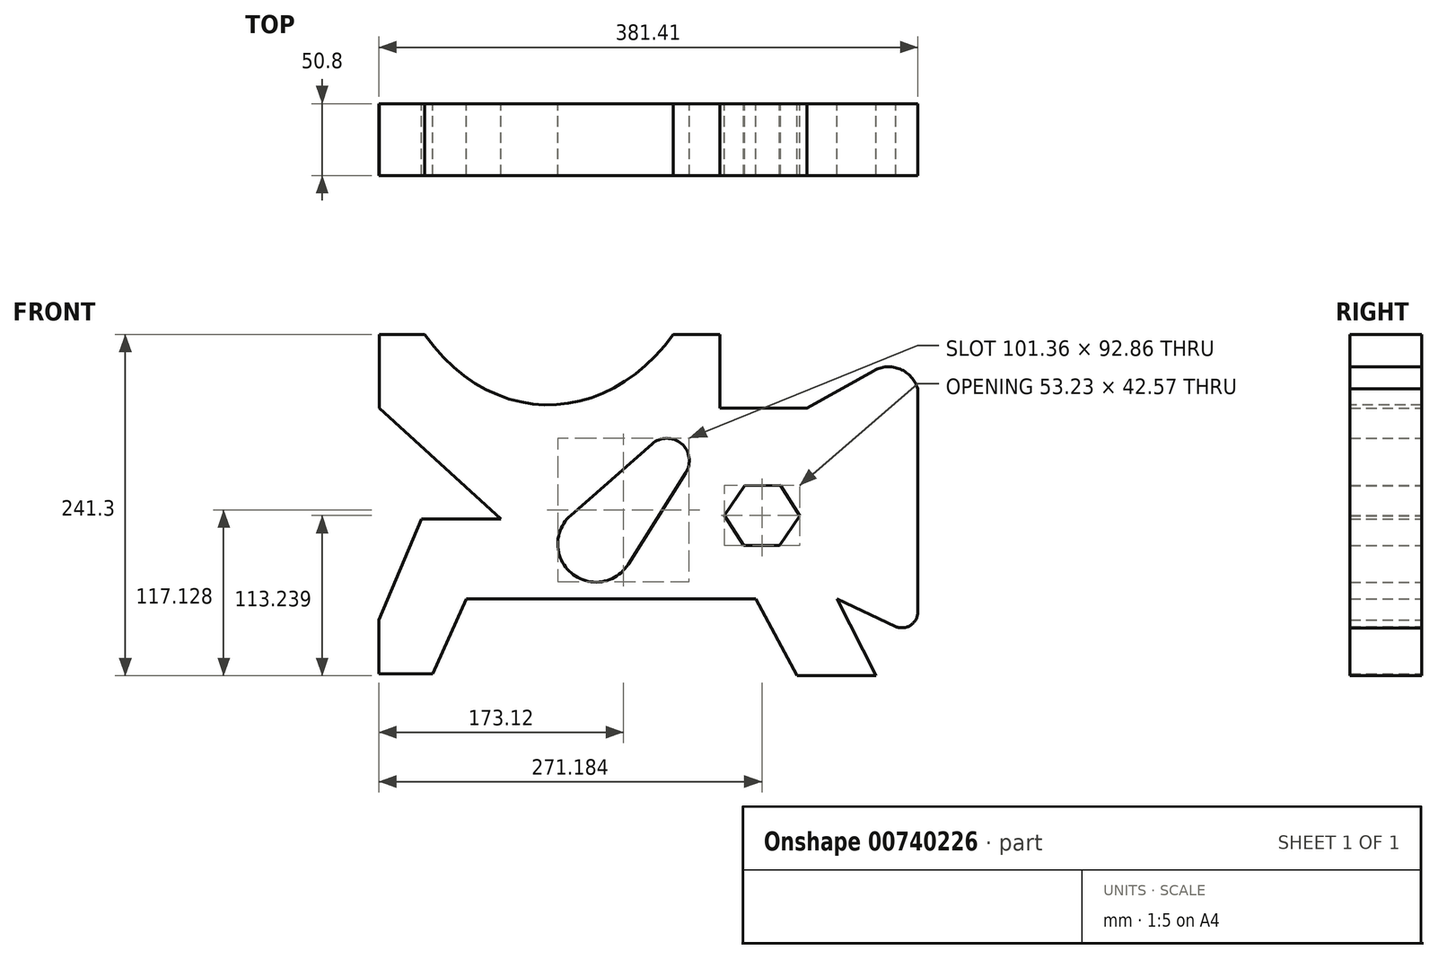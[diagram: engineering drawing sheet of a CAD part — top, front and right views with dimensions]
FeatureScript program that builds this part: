
annotation { "Feature Type Name" : "Feature", "Feature Type Description" : "" }
export const myFeature = defineFeature(function(context is Context, id is Id, definition is map)
    precondition{}
    {
        {
            var Q0;
            Q0=qCreatedBy(makeId("Front.planeOp"),FACE);
            var sketch = newSketch(context, id + "F0", { "sketchPlane" : qUnion([Q0])});
            skPoint(sketch, "E0.middle", {"position": v(-76.03, 243.1) * mm});
            skLineSegment(sketch, "E1", {"start": v(-266.94, 123.7) * mm, "end": v(-266.94, 161.8) * mm});
            skLineSegment(sketch, "E2", {"start": v(-266.94, 123.7) * mm, "end": v(-228.84, 123.7) * mm});
            skLineSegment(sketch, "E3", {"start": v(-228.84, 123.7) * mm, "end": v(-205, 176.8) * mm});
            skLineSegment(sketch, "E4", {"start": v(-266.94, 161.8) * mm, "end": v(-236.71, 233.26) * mm});
            skLineSegment(sketch, "E5", {"start": v(-236.71, 233.26) * mm, "end": v(-180.58, 233.26) * mm});
            skLineSegment(sketch, "E6", {"start": v(-180.58, 233.26) * mm, "end": v(-266.53, 311.7) * mm});
            skLineSegment(sketch, "E7", {"start": v(-266.53, 311.7) * mm, "end": v(-266.53, 363.76) * mm});
            skLineSegment(sketch, "E8", {"start": v(-266.53, 363.76) * mm, "end": v(-234.48, 363.76) * mm});
            skFitSpline(sketch, "E9", {"points": [v(-234.48, 363.76) * mm, v(-58.6, 363.76) * mm], "startDerivative": vector(146.16, -206.02) * mm, "endDerivative": vector(136.89, 191.75) * mm});
            skLineSegment(sketch, "E10", {"start": v(-58.6, 363.76) * mm, "end": v(-25.53, 363.76) * mm});
            skLineSegment(sketch, "E11", {"start": v(-25.53, 363.76) * mm, "end": v(-25.53, 311.7) * mm});
            skLineSegment(sketch, "E12", {"start": v(-25.53, 311.7) * mm, "end": v(36.19, 311.7) * mm});
            skLineSegment(sketch, "E13", {"start": v(83.32, 338.14) * mm, "end": v(36.19, 311.7) * mm});
            skArc(sketch, "E14", {"start": v(83.32, 338.14) * mm, "mid": v(102.02, 339.25) * mm, "end": v(114.47, 325.25) * mm});
            skLineSegment(sketch, "E15", {"start": v(114.47, 325.25) * mm, "end": v(114.47, 167.48) * mm});
            skArc(sketch, "E16", {"start": v(114.47, 167.48) * mm, "mid": v(109.5, 158.16) * mm, "end": v(99, 157.1) * mm});
            skLineSegment(sketch, "E17", {"start": v(99, 157.1) * mm, "end": v(57.48, 176.8) * mm});
            skLineSegment(sketch, "E18", {"start": v(57.48, 176.8) * mm, "end": v(84.93, 122.46) * mm});
            skLineSegment(sketch, "E19", {"start": v(84.93, 122.46) * mm, "end": v(28.95, 122.46) * mm});
            skLineSegment(sketch, "E20", {"start": v(28.95, 122.46) * mm, "end": v(0, 176.8) * mm});
            skLineSegment(sketch, "E21", {"start": v(-205, 176.8) * mm, "end": v(0, 176.8) * mm});
            skLineSegment(sketch, "E22", {"start": v(-73.5, 286.34) * mm, "end": v(-131.05, 235.9) * mm});
            skLineSegment(sketch, "E23", {"start": v(-90.41, 201.21) * mm, "end": v(-49.64, 265.97) * mm});
            skArc(sketch, "E24", {"start": v(-73.5, 286.34) * mm, "mid": v(-52.77, 286.48) * mm, "end": v(-49.64, 265.97) * mm});
            skArc(sketch, "E25", {"start": v(-131.05, 235.9) * mm, "mid": v(-130.78, 195.06) * mm, "end": v(-90.41, 201.21) * mm});
            skLineSegment(sketch, "E26", {"start": v(16.74, 214.41) * mm, "end": v(-8.66, 214.41) * mm});
            skLineSegment(sketch, "E27", {"start": v(-8.66, 214.41) * mm, "end": v(-22.37, 235.8) * mm});
            skLineSegment(sketch, "E28", {"start": v(-22.37, 235.8) * mm, "end": v(-8.14, 256.83) * mm});
            skLineSegment(sketch, "E29", {"start": v(-8.14, 256.83) * mm, "end": v(17.26, 256.98) * mm});
            skLineSegment(sketch, "E30", {"start": v(16.74, 214.41) * mm, "end": v(30.86, 235.53) * mm});
            skLineSegment(sketch, "E31", {"start": v(30.86, 235.53) * mm, "end": v(17.26, 256.98) * mm});
            skSolve(sketch);
        }
        {
            var Q0;
            Q0 = qSketchRegion(id + "F0", true);
            extrude(context, id + "F1", {"entities" : qUnion([Q0]), "endBound" : BoundingType.SYMMETRIC, "depth" : 50.8 * mm, "offsetDistance" : 25.4 * mm});
        }
    });
